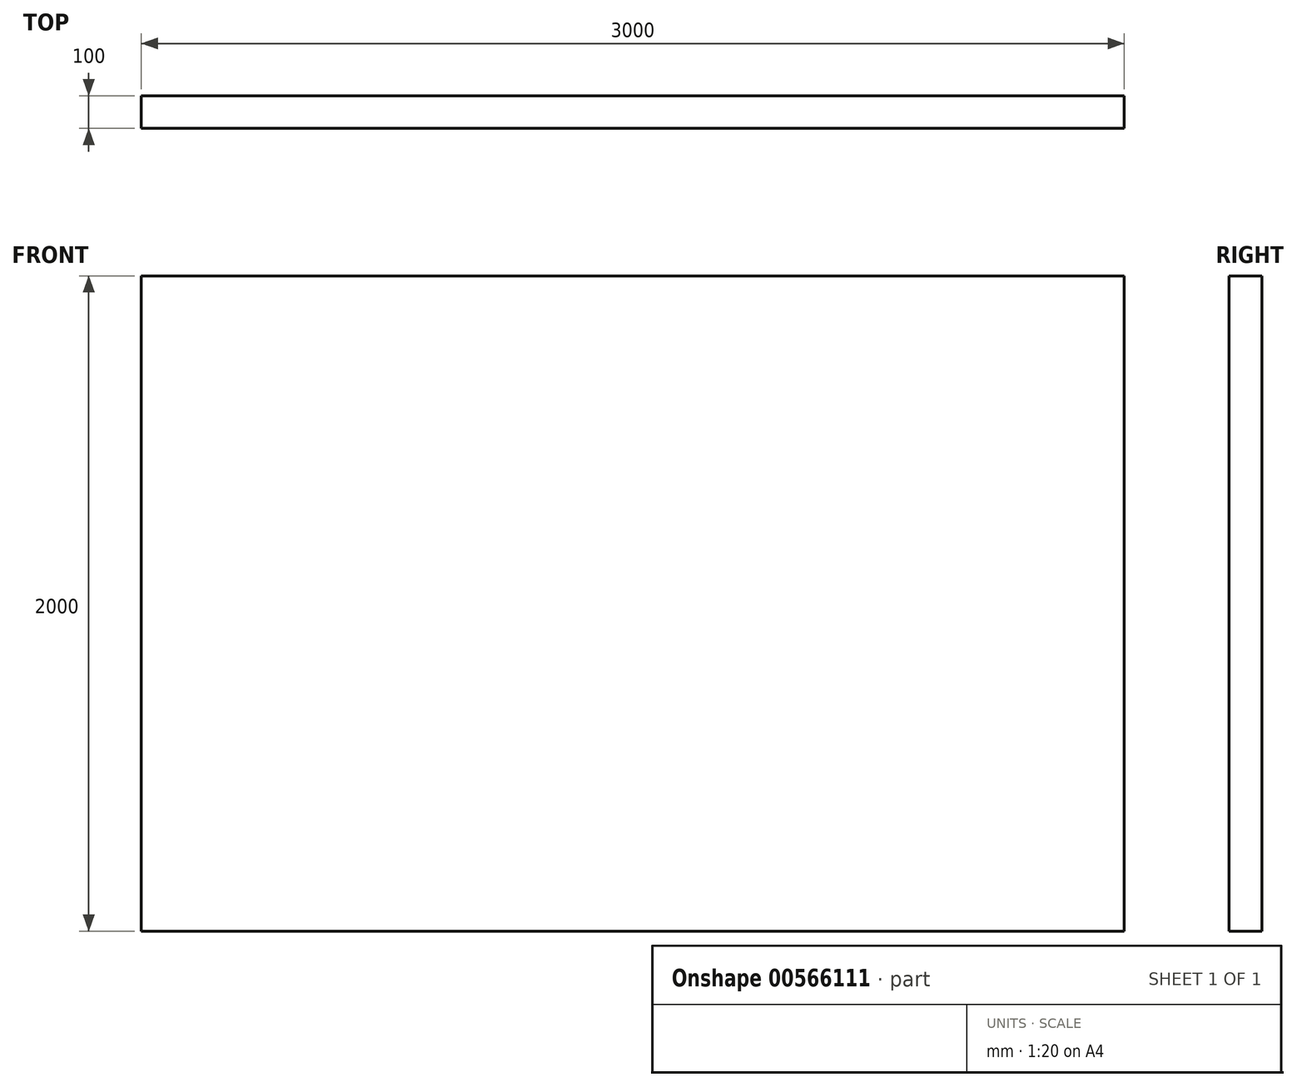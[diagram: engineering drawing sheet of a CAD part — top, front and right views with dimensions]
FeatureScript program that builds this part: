
annotation { "Feature Type Name" : "Feature", "Feature Type Description" : "" }
export const myFeature = defineFeature(function(context is Context, id is Id, definition is map)
    precondition{}
    {
        {
            var Q0;
            Q0=qCreatedBy(makeId("Front.planeOp"),FACE);
            var sketch = newSketch(context, id + "F0", { "sketchPlane" : qUnion([Q0])});
            skLineSegment(sketch, "E0.bottom", {"start": v(1500, -1000) * mm, "end": v(-1500, -1000) * mm});
            skLineSegment(sketch, "E0.top", {"start": v(1500, 1000) * mm, "end": v(-1500, 1000) * mm});
            skLineSegment(sketch, "E0.left", {"start": v(1500, -1000) * mm, "end": v(1500, 1000) * mm});
            skLineSegment(sketch, "E0.right", {"start": v(-1500, -1000) * mm, "end": v(-1500, 1000) * mm});
            skPoint(sketch, "E0.middle", {"position": v(0, 0) * mm});
            skSolve(sketch);
        }
        {
            var Q0;
            Q0=makeQuery(id+"F0.imprint","IMPRINT",FACE,{"disambiguationData":[TD([[makeQuery(id+"F0.imprint","IMPRINT",EDGE,{"derivedFrom":sQuery(id+"F0.wireOp",EDGE,"E0.bottom")}),-1.0]])]});
            extrude(context, id + "F1", {"entities" : qUnion([Q0]), "depth" : 100 * mm, "offsetDistance" : 25 * mm});
        }
    });
